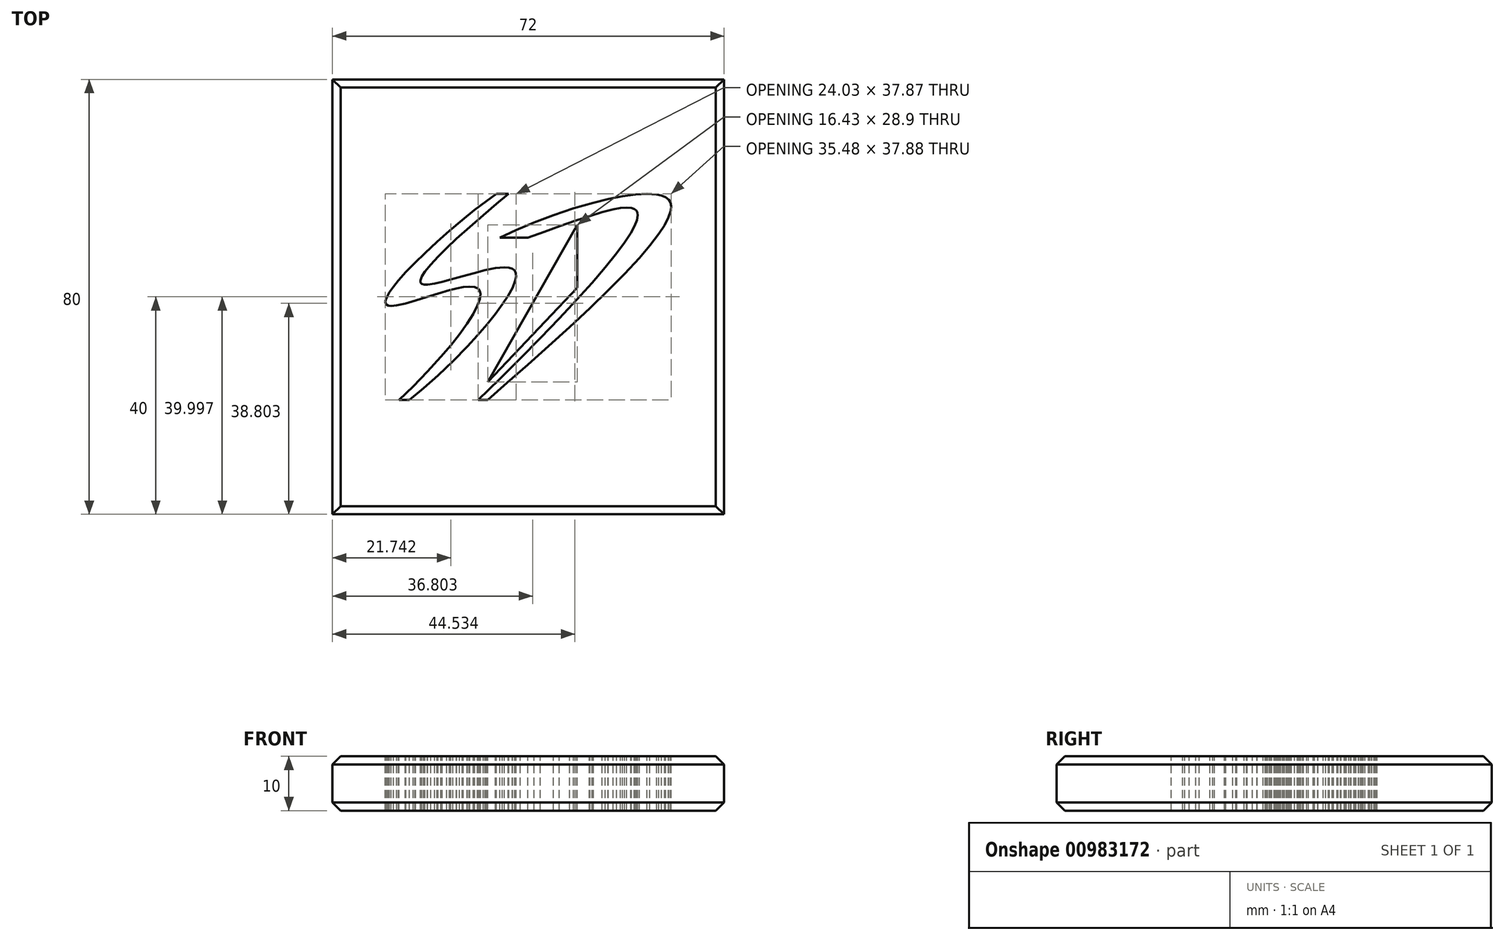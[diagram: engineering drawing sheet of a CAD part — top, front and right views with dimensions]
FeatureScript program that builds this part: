
annotation { "Feature Type Name" : "Feature", "Feature Type Description" : "" }
export const myFeature = defineFeature(function(context is Context, id is Id, definition is map)
    precondition{}
    {
        {
            var Q0;
            Q0=qCreatedBy(makeId("Top.planeOp"),FACE);
            var sketch = newSketch(context, id + "F0", { "sketchPlane" : qUnion([Q0])});
            skLineSegment(sketch, "E0.bottom", {"start": v(36, 40) * mm, "end": v(-36, 40) * mm});
            skLineSegment(sketch, "E0.top", {"start": v(36, -40) * mm, "end": v(-36, -40) * mm});
            skLineSegment(sketch, "E0.left", {"start": v(36, 40) * mm, "end": v(36, -40) * mm});
            skLineSegment(sketch, "E0.right", {"start": v(-36, 40) * mm, "end": v(-36, -40) * mm});
            skPoint(sketch, "E0.middle", {"position": v(0, 0) * mm});
            skLineSegment(sketch, "E1", {"start": v(0, 16.9) * mm, "end": v(0, 56.26) * mm, "construction": true});
            skLineSegment(sketch, "E2", {"start": v(-10, 42.81) * mm, "end": v(-10, 31.84) * mm, "construction": true});
            skArc(sketch, "E3", {"start": v(-10, 40) * mm, "mid": v(0, 50) * mm, "end": v(10, 40) * mm});
            skArc(sketch, "E4.0", {"start": v(-7, 40) * mm, "mid": v(0, 47) * mm, "end": v(7, 40) * mm});
            skSolve(sketch);
        }
        {
            var Q0;
            {var subQ0=sQuery(id+"F0.wireOp",EDGE,"E3");Q0=makeQuery(id+"F0.imprint","IMPRINT",FACE,{"disambiguationData":[TD([[makeQuery(id+"F0.imprint","IMPRINT",EDGE,{"derivedFrom":subQ0}),-1.0]])]});}
            var Q1;
            Q1=makeQuery(id+"F0.imprint","IMPRINT",FACE,{"disambiguationData":[TD([[makeQuery(id+"F0.imprint","IMPRINT",EDGE,{"derivedFrom":sQuery(id+"F0.wireOp",EDGE,"E0.top")}),-1.0]])]});
            extrude(context, id + "F1", {"entities" : qUnion([Q0, Q1]), "depth" : 10 * mm, "offsetDistance" : 25 * mm});
        }
        {
            var Q0;
            Q0=makeQuery(id+"F1.opExtrude","CAP_FACE",FACE,{"disambiguationData":[OSD([sQuery(id+"F0.wireOp",EDGE,"E0.bottom"),sQuery(id+"F0.wireOp",EDGE,"E0.top"),sQuery(id+"F0.wireOp",EDGE,"E0.left"),sQuery(id+"F0.wireOp",EDGE,"E0.right"),sQuery(id+"F0.wireOp",EDGE,"E3"),sQuery(id+"F0.wireOp",EDGE,"E4.0")])],"isStart":false});
            var Q1;
            Q1=makeQuery(id+"F1.opExtrude","CAP_FACE",FACE,{"disambiguationData":[OSD([sQuery(id+"F0.wireOp",EDGE,"E0.bottom"),sQuery(id+"F0.wireOp",EDGE,"E0.top"),sQuery(id+"F0.wireOp",EDGE,"E0.left"),sQuery(id+"F0.wireOp",EDGE,"E0.right"),sQuery(id+"F0.wireOp",EDGE,"E3"),sQuery(id+"F0.wireOp",EDGE,"E4.0")])],"isStart":true});
            chamfer(context, id + "F2", {"entities" : qUnion([Q0, Q1]), "width" : 1.5 * mm, "tangentPropagation" : true});
        }
        {
            var Q0;
            Q0=makeQuery(id+"F1.opExtrude","CAP_FACE",FACE,{"disambiguationData":[OSD([sQuery(id+"F0.wireOp",EDGE,"E0.bottom"),sQuery(id+"F0.wireOp",EDGE,"E0.top"),sQuery(id+"F0.wireOp",EDGE,"E0.left"),sQuery(id+"F0.wireOp",EDGE,"E0.right"),sQuery(id+"F0.wireOp",EDGE,"E3"),sQuery(id+"F0.wireOp",EDGE,"E4.0")])],"isStart":false});
            var sketch = newSketch(context, id + "F3", { "sketchPlane" : qUnion([Q0])});
            skLineSegment(sketch, "E5", {"start": v(-7.41, -15.65) * mm, "end": v(9.02, 1.69) * mm});
            skLineSegment(sketch, "E6", {"start": v(9.02, 13.25) * mm, "end": v(-7.41, -15.65) * mm});
            skLineSegment(sketch, "E7", {"start": v(9.02, 13.25) * mm, "end": v(9.02, 1.69) * mm});
            skLineSegment(sketch, "E8", {"start": v(-0.04, 10.9) * mm, "end": v(2.96, 11.98) * mm});
            skLineSegment(sketch, "E9", {"start": v(2.96, 11.98) * mm, "end": v(5.87, 13.02) * mm});
            skLineSegment(sketch, "E10", {"start": v(5.87, 13.02) * mm, "end": v(8.64, 14) * mm});
            skLineSegment(sketch, "E11", {"start": v(8.64, 14) * mm, "end": v(11.21, 14.85) * mm});
            skLineSegment(sketch, "E12", {"start": v(11.21, 14.85) * mm, "end": v(13.55, 15.56) * mm});
            skLineSegment(sketch, "E13", {"start": v(13.55, 15.56) * mm, "end": v(15.61, 16.08) * mm});
            skLineSegment(sketch, "E14", {"start": v(15.61, 16.08) * mm, "end": v(16.94, 16.32) * mm});
            skLineSegment(sketch, "E15", {"start": v(16.94, 16.32) * mm, "end": v(18.07, 16.4) * mm});
            skLineSegment(sketch, "E16", {"start": v(18.07, 16.4) * mm, "end": v(18.97, 16.34) * mm});
            skLineSegment(sketch, "E17", {"start": v(18.97, 16.34) * mm, "end": v(19.49, 16.17) * mm});
            skLineSegment(sketch, "E18", {"start": v(19.49, 16.17) * mm, "end": v(19.86, 15.9) * mm});
            skLineSegment(sketch, "E19", {"start": v(19.86, 15.9) * mm, "end": v(20.08, 15.5) * mm});
            skLineSegment(sketch, "E20", {"start": v(20.08, 15.5) * mm, "end": v(20.14, 15) * mm});
            skLineSegment(sketch, "E21", {"start": v(20.14, 15) * mm, "end": v(19.98, 14.11) * mm});
            skLineSegment(sketch, "E22", {"start": v(19.98, 14.11) * mm, "end": v(19.54, 13.01) * mm});
            skLineSegment(sketch, "E23", {"start": v(19.54, 13.01) * mm, "end": v(18.85, 11.73) * mm});
            skLineSegment(sketch, "E24", {"start": v(18.85, 11.73) * mm, "end": v(17.71, 9.98) * mm});
            skLineSegment(sketch, "E25", {"start": v(17.71, 9.98) * mm, "end": v(16.26, 8.01) * mm});
            skLineSegment(sketch, "E26", {"start": v(16.26, 8.01) * mm, "end": v(14.17, 5.4) * mm});
            skLineSegment(sketch, "E27", {"start": v(14.17, 5.4) * mm, "end": v(11.73, 2.56) * mm});
            skLineSegment(sketch, "E28", {"start": v(11.73, 2.56) * mm, "end": v(8.97, -0.5) * mm});
            skLineSegment(sketch, "E29", {"start": v(8.97, -0.5) * mm, "end": v(5.72, -3.98) * mm});
            skLineSegment(sketch, "E30", {"start": v(5.72, -3.98) * mm, "end": v(2.22, -7.6) * mm});
            skLineSegment(sketch, "E31", {"start": v(2.22, -7.6) * mm, "end": v(-1.47, -11.34) * mm});
            skLineSegment(sketch, "E32", {"start": v(-1.47, -11.34) * mm, "end": v(-5.3, -15.13) * mm});
            skLineSegment(sketch, "E33", {"start": v(-5.3, -15.13) * mm, "end": v(-9.2, -18.94) * mm});
            skLineSegment(sketch, "E34", {"start": v(-3.62, 18.93) * mm, "end": v(-5.84, 17.09) * mm});
            skLineSegment(sketch, "E35", {"start": v(-5.84, 17.09) * mm, "end": v(-8.27, 15.03) * mm});
            skLineSegment(sketch, "E36", {"start": v(-8.27, 15.03) * mm, "end": v(-10.76, 12.86) * mm});
            skLineSegment(sketch, "E37", {"start": v(-10.76, 12.86) * mm, "end": v(-13.2, 10.66) * mm});
            skLineSegment(sketch, "E38", {"start": v(-13.2, 10.66) * mm, "end": v(-14.99, 8.98) * mm});
            skLineSegment(sketch, "E39", {"start": v(-14.99, 8.98) * mm, "end": v(-16.58, 7.4) * mm});
            skLineSegment(sketch, "E40", {"start": v(-16.58, 7.4) * mm, "end": v(-17.94, 5.94) * mm});
            skLineSegment(sketch, "E41", {"start": v(-17.94, 5.94) * mm, "end": v(-18.97, 4.66) * mm});
            skLineSegment(sketch, "E42", {"start": v(-18.97, 4.66) * mm, "end": v(-19.56, 3.74) * mm});
            skLineSegment(sketch, "E43", {"start": v(-19.56, 3.74) * mm, "end": v(-19.83, 3.02) * mm});
            skLineSegment(sketch, "E44", {"start": v(-19.83, 3.02) * mm, "end": v(-19.8, 2.62) * mm});
            skLineSegment(sketch, "E45", {"start": v(-19.8, 2.62) * mm, "end": v(-19.56, 2.36) * mm});
            skLineSegment(sketch, "E46", {"start": v(-19.56, 2.36) * mm, "end": v(-19.12, 2.24) * mm});
            skLineSegment(sketch, "E47", {"start": v(-19.12, 2.24) * mm, "end": v(-18.5, 2.24) * mm});
            skLineSegment(sketch, "E48", {"start": v(-18.5, 2.24) * mm, "end": v(-17.22, 2.43) * mm});
            skLineSegment(sketch, "E49", {"start": v(-17.22, 2.43) * mm, "end": v(-15.8, 2.75) * mm});
            skLineSegment(sketch, "E50", {"start": v(-15.8, 2.75) * mm, "end": v(-14.22, 3.18) * mm});
            skLineSegment(sketch, "E51", {"start": v(-14.22, 3.18) * mm, "end": v(-12.14, 3.77) * mm});
            skLineSegment(sketch, "E52", {"start": v(-12.14, 3.77) * mm, "end": v(-10, 4.36) * mm});
            skLineSegment(sketch, "E53", {"start": v(-10, 4.36) * mm, "end": v(-7.93, 4.9) * mm});
            skLineSegment(sketch, "E54", {"start": v(-7.93, 4.9) * mm, "end": v(-6.02, 5.27) * mm});
            skLineSegment(sketch, "E55", {"start": v(-6.02, 5.27) * mm, "end": v(-4.4, 5.42) * mm});
            skLineSegment(sketch, "E56", {"start": v(-4.4, 5.42) * mm, "end": v(-3.57, 5.37) * mm});
            skLineSegment(sketch, "E57", {"start": v(-3.57, 5.37) * mm, "end": v(-2.93, 5.18) * mm});
            skLineSegment(sketch, "E58", {"start": v(-2.93, 5.18) * mm, "end": v(-2.5, 4.84) * mm});
            skLineSegment(sketch, "E59", {"start": v(-2.5, 4.84) * mm, "end": v(-2.28, 4.35) * mm});
            skLineSegment(sketch, "E60", {"start": v(-2.28, 4.35) * mm, "end": v(-2.24, 3.72) * mm});
            skLineSegment(sketch, "E61", {"start": v(-2.24, 3.72) * mm, "end": v(-2.4, 2.96) * mm});
            skLineSegment(sketch, "E62", {"start": v(-2.4, 2.96) * mm, "end": v(-2.88, 1.7) * mm});
            skLineSegment(sketch, "E63", {"start": v(-2.88, 1.7) * mm, "end": v(-3.68, 0.24) * mm});
            skLineSegment(sketch, "E64", {"start": v(-3.68, 0.24) * mm, "end": v(-4.74, -1.39) * mm});
            skLineSegment(sketch, "E65", {"start": v(-4.74, -1.39) * mm, "end": v(-6.03, -3.14) * mm});
            skLineSegment(sketch, "E66", {"start": v(-6.03, -3.14) * mm, "end": v(-7.6, -5.08) * mm});
            skLineSegment(sketch, "E67", {"start": v(-7.6, -5.08) * mm, "end": v(-9.33, -7.08) * mm});
            skLineSegment(sketch, "E68", {"start": v(-9.33, -7.08) * mm, "end": v(-11.2, -9.12) * mm});
            skLineSegment(sketch, "E69", {"start": v(-11.2, -9.12) * mm, "end": v(-13.85, -11.82) * mm});
            skLineSegment(sketch, "E70", {"start": v(-13.85, -11.82) * mm, "end": v(-16.57, -14.42) * mm});
            skLineSegment(sketch, "E71", {"start": v(-16.57, -14.42) * mm, "end": v(-19.26, -16.83) * mm});
            skLineSegment(sketch, "E72", {"start": v(-19.26, -16.83) * mm, "end": v(-21.84, -18.94) * mm});
            skLineSegment(sketch, "E73", {"start": v(-5.86, 18.93) * mm, "end": v(-7.77, 17.58) * mm});
            skLineSegment(sketch, "E74", {"start": v(-7.77, 17.58) * mm, "end": v(-9.9, 15.96) * mm});
            skLineSegment(sketch, "E75", {"start": v(-9.9, 15.96) * mm, "end": v(-12.15, 14.14) * mm});
            skLineSegment(sketch, "E76", {"start": v(-12.15, 14.14) * mm, "end": v(-14.48, 12.17) * mm});
            skLineSegment(sketch, "E77", {"start": v(-14.48, 12.17) * mm, "end": v(-16.79, 10.12) * mm});
            skLineSegment(sketch, "E78", {"start": v(-16.79, 10.12) * mm, "end": v(-19.01, 8.06) * mm});
            skLineSegment(sketch, "E79", {"start": v(-19.01, 8.06) * mm, "end": v(-20.83, 6.28) * mm});
            skLineSegment(sketch, "E80", {"start": v(-20.83, 6.28) * mm, "end": v(-22.48, 4.57) * mm});
            skLineSegment(sketch, "E81", {"start": v(-22.48, 4.57) * mm, "end": v(-23.89, 3) * mm});
            skLineSegment(sketch, "E82", {"start": v(-23.89, 3) * mm, "end": v(-24.8, 1.86) * mm});
            skLineSegment(sketch, "E83", {"start": v(-24.8, 1.86) * mm, "end": v(-25.52, 0.85) * mm});
            skLineSegment(sketch, "E84", {"start": v(-25.52, 0.85) * mm, "end": v(-26, -0.01) * mm});
            skLineSegment(sketch, "E85", {"start": v(-26, -0.01) * mm, "end": v(-26.2, -0.49) * mm});
            skLineSegment(sketch, "E86", {"start": v(-26.2, -0.49) * mm, "end": v(-26.27, -0.89) * mm});
            skLineSegment(sketch, "E87", {"start": v(-26.27, -0.89) * mm, "end": v(-26.23, -1.2) * mm});
            skLineSegment(sketch, "E88", {"start": v(-26.23, -1.2) * mm, "end": v(-26.06, -1.44) * mm});
            skLineSegment(sketch, "E89", {"start": v(-26.06, -1.44) * mm, "end": v(-25.73, -1.6) * mm});
            skLineSegment(sketch, "E90", {"start": v(-25.73, -1.6) * mm, "end": v(-25.24, -1.66) * mm});
            skLineSegment(sketch, "E91", {"start": v(-25.24, -1.66) * mm, "end": v(-24.2, -1.56) * mm});
            skLineSegment(sketch, "E92", {"start": v(-24.2, -1.56) * mm, "end": v(-22.6, -1.21) * mm});
            skLineSegment(sketch, "E93", {"start": v(-22.6, -1.21) * mm, "end": v(-20.72, -0.68) * mm});
            skLineSegment(sketch, "E94", {"start": v(-20.72, -0.68) * mm, "end": v(-18.67, -0.04) * mm});
            skLineSegment(sketch, "E95", {"start": v(-18.67, -0.04) * mm, "end": v(-16.56, 0.61) * mm});
            skLineSegment(sketch, "E96", {"start": v(-16.56, 0.61) * mm, "end": v(-14.5, 1.2) * mm});
            skLineSegment(sketch, "E97", {"start": v(-14.5, 1.2) * mm, "end": v(-13.15, 1.54) * mm});
            skLineSegment(sketch, "E98", {"start": v(-13.15, 1.54) * mm, "end": v(-11.92, 1.78) * mm});
            skLineSegment(sketch, "E99", {"start": v(-11.92, 1.78) * mm, "end": v(-10.85, 1.89) * mm});
            skLineSegment(sketch, "E100", {"start": v(-10.85, 1.89) * mm, "end": v(-9.84, 1.82) * mm});
            skLineSegment(sketch, "E101", {"start": v(-9.84, 1.82) * mm, "end": v(-9.16, 1.5) * mm});
            skLineSegment(sketch, "E102", {"start": v(-9.16, 1.5) * mm, "end": v(-8.87, 1.07) * mm});
            skLineSegment(sketch, "E103", {"start": v(-8.87, 1.07) * mm, "end": v(-8.77, 0.51) * mm});
            skLineSegment(sketch, "E104", {"start": v(-8.77, 0.51) * mm, "end": v(-8.9, -0.43) * mm});
            skLineSegment(sketch, "E105", {"start": v(-8.9, -0.43) * mm, "end": v(-9.31, -1.57) * mm});
            skLineSegment(sketch, "E106", {"start": v(-9.31, -1.57) * mm, "end": v(-10.13, -3.16) * mm});
            skLineSegment(sketch, "E107", {"start": v(-10.13, -3.16) * mm, "end": v(-11.26, -4.94) * mm});
            skLineSegment(sketch, "E108", {"start": v(-11.26, -4.94) * mm, "end": v(-12.65, -6.88) * mm});
            skLineSegment(sketch, "E109", {"start": v(-12.65, -6.88) * mm, "end": v(-14.26, -8.92) * mm});
            skLineSegment(sketch, "E110", {"start": v(-14.26, -8.92) * mm, "end": v(-16.04, -11.02) * mm});
            skLineSegment(sketch, "E111", {"start": v(-16.04, -11.02) * mm, "end": v(-18.55, -13.78) * mm});
            skLineSegment(sketch, "E112", {"start": v(-18.55, -13.78) * mm, "end": v(-21.15, -16.45) * mm});
            skLineSegment(sketch, "E113", {"start": v(-21.15, -16.45) * mm, "end": v(-23.75, -18.94) * mm});
            skLineSegment(sketch, "E114", {"start": v(-5.23, 10.9) * mm, "end": v(-2.25, 12.31) * mm});
            skLineSegment(sketch, "E115", {"start": v(-2.25, 12.31) * mm, "end": v(1.09, 13.71) * mm});
            skLineSegment(sketch, "E116", {"start": v(1.09, 13.71) * mm, "end": v(4.66, 15.04) * mm});
            skLineSegment(sketch, "E117", {"start": v(4.66, 15.04) * mm, "end": v(8.33, 16.26) * mm});
            skLineSegment(sketch, "E118", {"start": v(8.33, 16.26) * mm, "end": v(11.98, 17.3) * mm});
            skLineSegment(sketch, "E119", {"start": v(11.98, 17.3) * mm, "end": v(14.74, 17.98) * mm});
            skLineSegment(sketch, "E120", {"start": v(14.74, 17.98) * mm, "end": v(17.35, 18.49) * mm});
            skLineSegment(sketch, "E121", {"start": v(17.35, 18.49) * mm, "end": v(19.74, 18.82) * mm});
            skLineSegment(sketch, "E122", {"start": v(19.74, 18.82) * mm, "end": v(21.85, 18.94) * mm});
            skLineSegment(sketch, "E123", {"start": v(21.85, 18.94) * mm, "end": v(23.62, 18.83) * mm});
            skLineSegment(sketch, "E124", {"start": v(23.62, 18.83) * mm, "end": v(24.53, 18.63) * mm});
            skLineSegment(sketch, "E125", {"start": v(24.53, 18.63) * mm, "end": v(25.27, 18.32) * mm});
            skLineSegment(sketch, "E126", {"start": v(25.27, 18.32) * mm, "end": v(25.8, 17.9) * mm});
            skLineSegment(sketch, "E127", {"start": v(25.8, 17.9) * mm, "end": v(26.14, 17.35) * mm});
            skLineSegment(sketch, "E128", {"start": v(26.14, 17.35) * mm, "end": v(26.27, 16.69) * mm});
            skLineSegment(sketch, "E129", {"start": v(26.27, 16.69) * mm, "end": v(26.2, 15.91) * mm});
            skLineSegment(sketch, "E130", {"start": v(26.2, 15.91) * mm, "end": v(25.8, 14.65) * mm});
            skLineSegment(sketch, "E131", {"start": v(25.8, 14.65) * mm, "end": v(25.04, 13.19) * mm});
            skLineSegment(sketch, "E132", {"start": v(25.04, 13.19) * mm, "end": v(23.98, 11.56) * mm});
            skLineSegment(sketch, "E133", {"start": v(23.98, 11.56) * mm, "end": v(22.38, 9.45) * mm});
            skLineSegment(sketch, "E134", {"start": v(22.38, 9.45) * mm, "end": v(20.42, 7.16) * mm});
            skLineSegment(sketch, "E135", {"start": v(20.42, 7.16) * mm, "end": v(17.72, 4.23) * mm});
            skLineSegment(sketch, "E136", {"start": v(17.72, 4.23) * mm, "end": v(14.67, 1.15) * mm});
            skLineSegment(sketch, "E137", {"start": v(14.67, 1.15) * mm, "end": v(11.36, -2.05) * mm});
            skLineSegment(sketch, "E138", {"start": v(11.36, -2.05) * mm, "end": v(7.62, -5.54) * mm});
            skLineSegment(sketch, "E139", {"start": v(7.62, -5.54) * mm, "end": v(3.77, -9.04) * mm});
            skLineSegment(sketch, "E140", {"start": v(3.77, -9.04) * mm, "end": v(-0.1, -12.48) * mm});
            skLineSegment(sketch, "E141", {"start": v(-0.1, -12.48) * mm, "end": v(-3.87, -15.8) * mm});
            skLineSegment(sketch, "E142", {"start": v(-3.87, -15.8) * mm, "end": v(-7.47, -18.94) * mm});
            skLineSegment(sketch, "E143", {"start": v(-5.23, 10.9) * mm, "end": v(-0.04, 10.9) * mm});
            skLineSegment(sketch, "E144", {"start": v(-9.2, -18.94) * mm, "end": v(-7.47, -18.94) * mm});
            skLineSegment(sketch, "E145", {"start": v(-23.75, -18.94) * mm, "end": v(-21.84, -18.94) * mm});
            skLineSegment(sketch, "E146", {"start": v(-5.86, 18.93) * mm, "end": v(-3.62, 18.93) * mm});
            skSolve(sketch);
        }
        {
            var Q0;
            Q0 = qSketchRegion(id + "F3", true);
            extrude(context, id + "F4", {"entities" : qUnion([Q0]), "operationType" : NewBodyOperationType.REMOVE, "oppositeDirection" : true, "depth" : 10 * mm, "offsetDistance" : 25 * mm});
        }
    });
